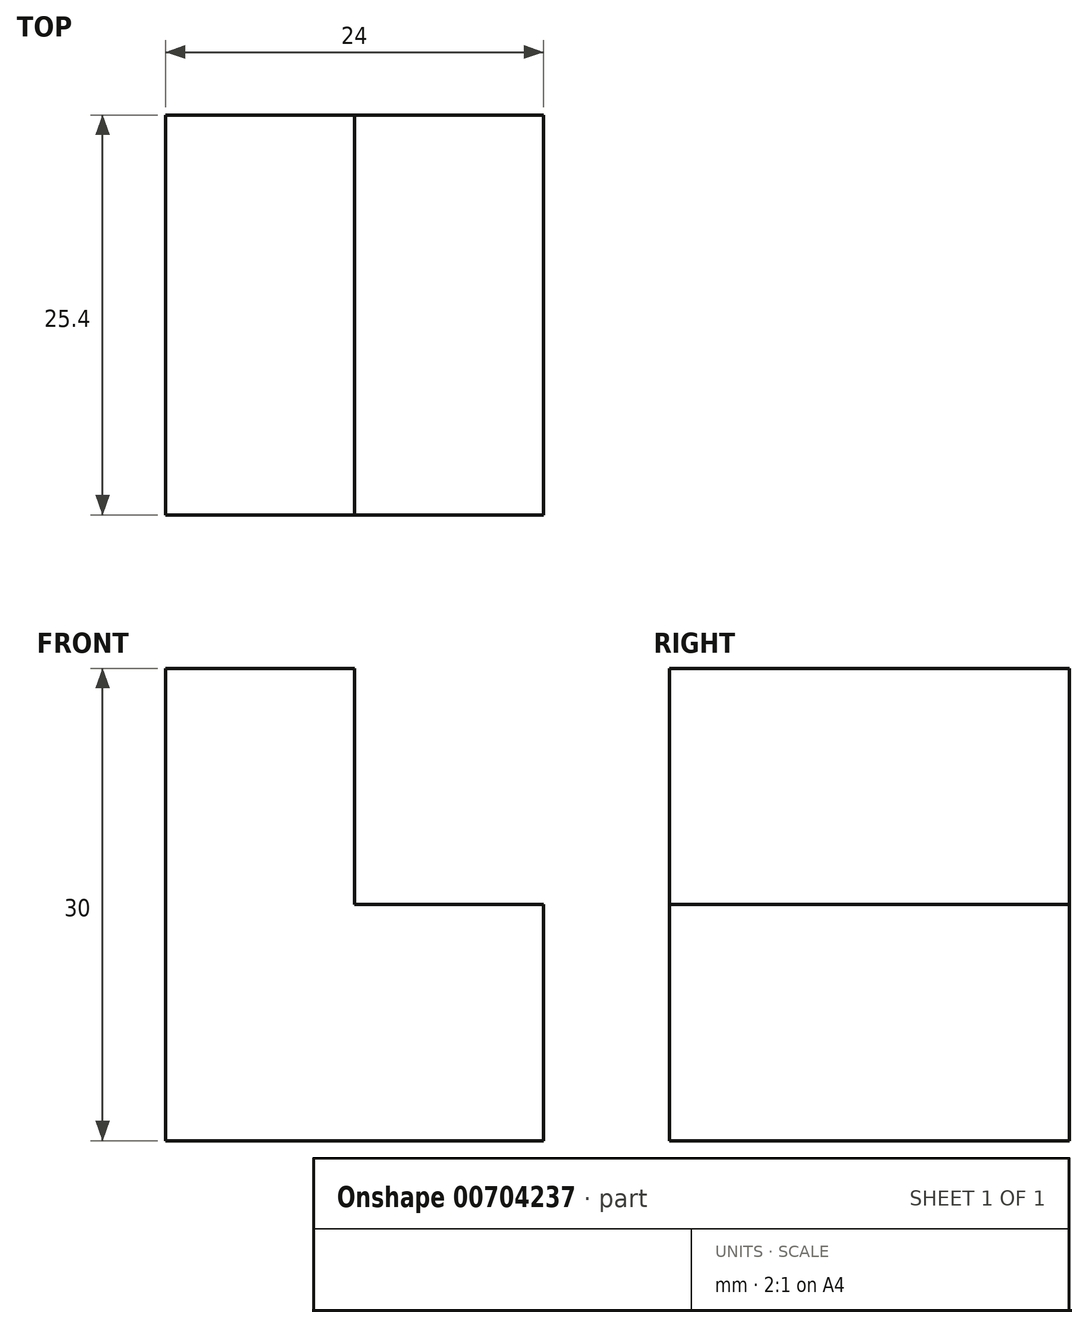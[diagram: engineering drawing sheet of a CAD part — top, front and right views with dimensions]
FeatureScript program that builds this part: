
annotation { "Feature Type Name" : "Feature", "Feature Type Description" : "" }
export const myFeature = defineFeature(function(context is Context, id is Id, definition is map)
    precondition{}
    {
        {
            var Q0;
            Q0=qCreatedBy(makeId("Front.planeOp"),FACE);
            var sketch = newSketch(context, id + "F0", { "sketchPlane" : qUnion([Q0])});
            skLineSegment(sketch, "E0", {"start": v(-12, 15) * mm, "end": v(0, 15) * mm});
            skLineSegment(sketch, "E1", {"start": v(-12, 15) * mm, "end": v(-12, -15) * mm});
            skLineSegment(sketch, "E2", {"start": v(-12, -15) * mm, "end": v(12, -15) * mm});
            skLineSegment(sketch, "E3", {"start": v(12, -15) * mm, "end": v(12, 0) * mm});
            skLineSegment(sketch, "E4", {"start": v(12, 0) * mm, "end": v(0, 0) * mm});
            skLineSegment(sketch, "E5", {"start": v(0, 0) * mm, "end": v(0, 15) * mm});
            skSolve(sketch);
        }
        {
            var Q0;
            Q0 = qSketchRegion(id + "F0", true);
            extrude(context, id + "F1", {"entities" : qUnion([Q0]), "depth" : 25.4 * mm, "offsetDistance" : 25.4 * mm});
        }
    });
